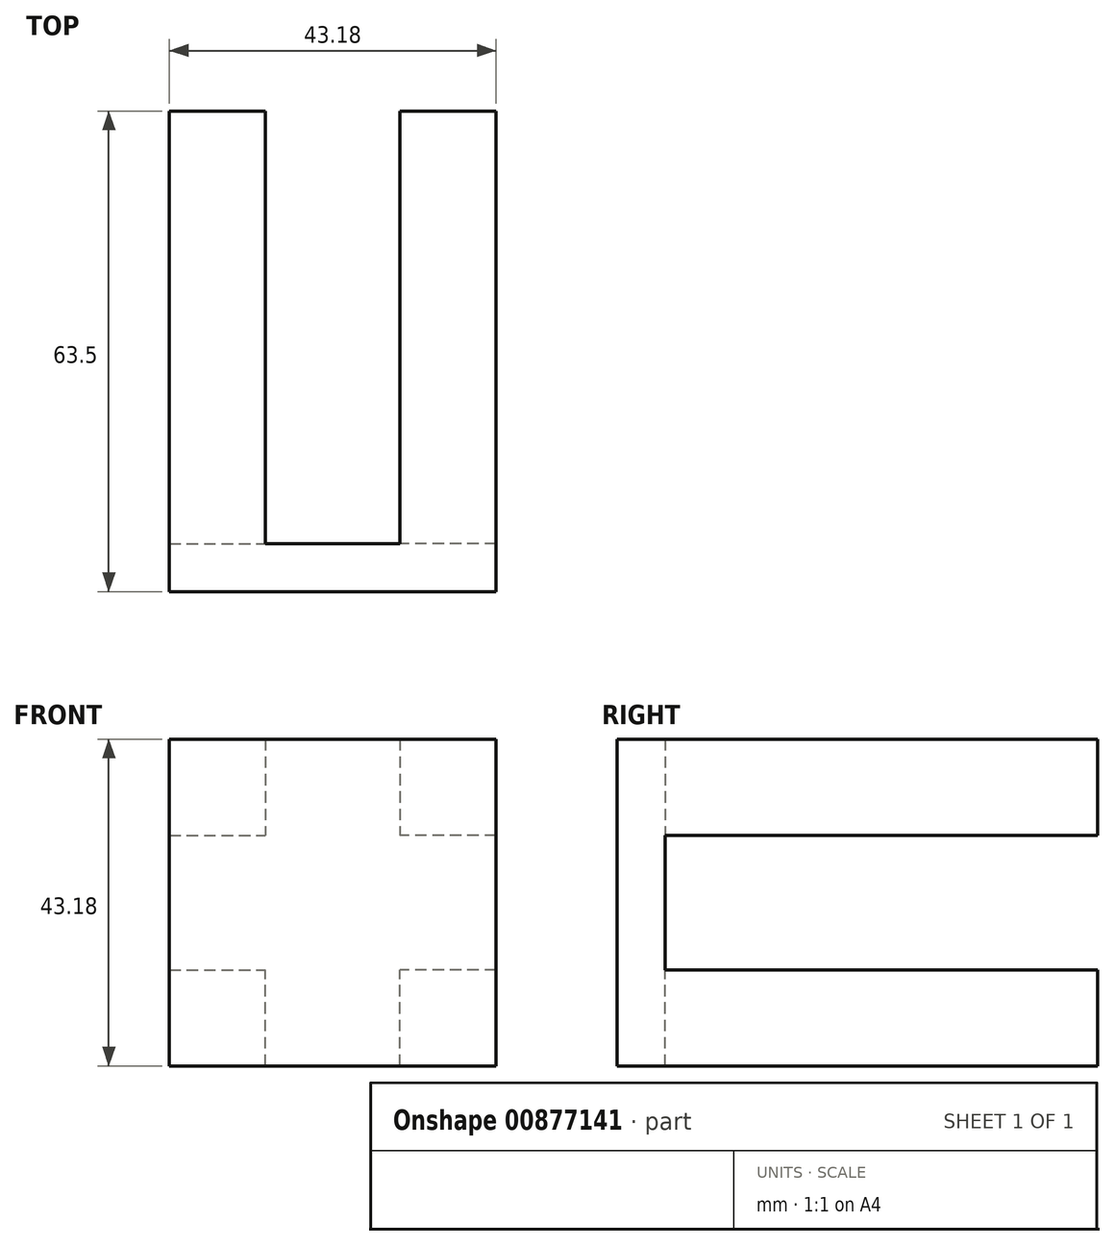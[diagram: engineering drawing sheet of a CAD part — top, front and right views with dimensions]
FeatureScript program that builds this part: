
annotation { "Feature Type Name" : "Feature", "Feature Type Description" : "" }
export const myFeature = defineFeature(function(context is Context, id is Id, definition is map)
    precondition{}
    {
        {
            var Q0;
            Q0=qCreatedBy(makeId("Front.planeOp"),FACE);
            var sketch = newSketch(context, id + "F0", { "sketchPlane" : qUnion([Q0])});
            skLineSegment(sketch, "E0.bottom", {"start": v(-131.6, 23.95) * mm, "end": v(-110, 23.95) * mm});
            skLineSegment(sketch, "E0.top", {"start": v(-131.6, -19.23) * mm, "end": v(-110, -19.23) * mm});
            skLineSegment(sketch, "E0.left", {"start": v(-131.6, 23.95) * mm, "end": v(-131.6, -19.23) * mm});
            skLineSegment(sketch, "E1.bottom", {"start": v(-131.6, 23.95) * mm, "end": v(-118.9, 23.95) * mm});
            skLineSegment(sketch, "E1.top", {"start": v(-131.6, 11.25) * mm, "end": v(-118.9, 11.25) * mm});
            skLineSegment(sketch, "E1.left", {"start": v(-131.6, 23.95) * mm, "end": v(-131.6, 11.25) * mm});
            skLineSegment(sketch, "E1.right", {"start": v(-118.9, 23.95) * mm, "end": v(-118.9, 11.25) * mm});
            skLineSegment(sketch, "E2.bottom", {"start": v(-131.6, -19.23) * mm, "end": v(-118.9, -19.23) * mm});
            skLineSegment(sketch, "E2.top", {"start": v(-131.6, -6.53) * mm, "end": v(-118.9, -6.53) * mm});
            skLineSegment(sketch, "E2.left", {"start": v(-131.6, -19.23) * mm, "end": v(-131.6, -6.53) * mm});
            skLineSegment(sketch, "E2.right", {"start": v(-118.9, -19.23) * mm, "end": v(-118.9, -6.53) * mm});
            skLineSegment(sketch, "E3.MirrorCS", {"start": v(-88.41, 23.95) * mm, "end": v(-88.41, 11.25) * mm});
            skLineSegment(sketch, "E4.MirrorCS", {"start": v(-88.41, -19.23) * mm, "end": v(-88.41, -6.53) * mm});
            skLineSegment(sketch, "E5.MirrorCS", {"start": v(-88.41, -6.53) * mm, "end": v(-101.11, -6.53) * mm});
            skLineSegment(sketch, "E6.MirrorCS", {"start": v(-88.41, -19.23) * mm, "end": v(-101.11, -19.23) * mm});
            skLineSegment(sketch, "E7.MirrorCS", {"start": v(-101.11, -19.23) * mm, "end": v(-101.11, -6.53) * mm});
            skLineSegment(sketch, "E8.MirrorCS", {"start": v(-88.41, 23.95) * mm, "end": v(-88.41, -19.23) * mm});
            skLineSegment(sketch, "E9.MirrorCS", {"start": v(-101.11, 23.95) * mm, "end": v(-101.11, 11.25) * mm});
            skLineSegment(sketch, "E10.MirrorCS", {"start": v(-88.41, -19.23) * mm, "end": v(-110, -19.23) * mm});
            skLineSegment(sketch, "E11.MirrorCS", {"start": v(-88.41, 11.25) * mm, "end": v(-101.11, 11.25) * mm});
            skLineSegment(sketch, "E12.MirrorCS", {"start": v(-88.41, 23.95) * mm, "end": v(-110, 23.95) * mm});
            skLineSegment(sketch, "E13.MirrorCS", {"start": v(-88.41, 23.95) * mm, "end": v(-101.11, 23.95) * mm});
            skSolve(sketch);
        }
        {
            var Q0;
            {var subQ8=sQuery(id+"F0.wireOp",EDGE,"E1.top");Q0=makeQuery(id+"F0.imprint","IMPRINT",FACE,{"disambiguationData":[TD([[makeQuery(id+"F0.imprint","IMPRINT",EDGE,{"derivedFrom":subQ8}),-1.0]])]});}
            extrude(context, id + "F1", {"entities" : qUnion([Q0]), "depth" : 6.35 * mm, "offsetDistance" : 25.4 * mm});
        }
        {
            var Q0;
            Q0=makeQuery(id+"F1.opExtrude","CAP_FACE",FACE,{"disambiguationData":[OSD([sQuery(id+"F0.wireOp",EDGE,"E0.bottom"),sQuery(id+"F0.wireOp",EDGE,"E0.top"),sQuery(id+"F0.wireOp",EDGE,"E0.left"),sQuery(id+"F0.wireOp",EDGE,"E1.top"),sQuery(id+"F0.wireOp",EDGE,"E1.right"),sQuery(id+"F0.wireOp",EDGE,"E2.top"),sQuery(id+"F0.wireOp",EDGE,"E2.right"),sQuery(id+"F0.wireOp",EDGE,"E5.MirrorCS"),sQuery(id+"F0.wireOp",EDGE,"E7.MirrorCS"),sQuery(id+"F0.wireOp",EDGE,"E8.MirrorCS"),sQuery(id+"F0.wireOp",EDGE,"E9.MirrorCS"),sQuery(id+"F0.wireOp",EDGE,"E10.MirrorCS"),sQuery(id+"F0.wireOp",EDGE,"E11.MirrorCS"),sQuery(id+"F0.wireOp",EDGE,"E12.MirrorCS")])],"isStart":false});
            var sketch = newSketch(context, id + "F2", { "sketchPlane" : qUnion([Q0])});
            skLineSegment(sketch, "E14.bottom", {"start": v(-118.9, 11.25) * mm, "end": v(-131.6, 11.25) * mm});
            skLineSegment(sketch, "E14.top", {"start": v(-118.9, 23.95) * mm, "end": v(-131.6, 23.95) * mm});
            skLineSegment(sketch, "E14.left", {"start": v(-118.9, 11.25) * mm, "end": v(-118.9, 23.95) * mm});
            skLineSegment(sketch, "E14.right", {"start": v(-131.6, 11.25) * mm, "end": v(-131.6, 23.95) * mm});
            skLineSegment(sketch, "E15.bottom", {"start": v(-101.11, 23.95) * mm, "end": v(-88.41, 23.95) * mm});
            skLineSegment(sketch, "E15.top", {"start": v(-101.11, 11.25) * mm, "end": v(-88.41, 11.25) * mm});
            skLineSegment(sketch, "E15.left", {"start": v(-101.11, 23.95) * mm, "end": v(-101.11, 11.25) * mm});
            skLineSegment(sketch, "E15.right", {"start": v(-88.41, 23.95) * mm, "end": v(-88.41, 11.25) * mm});
            skLineSegment(sketch, "E16.bottom", {"start": v(-88.41, -19.23) * mm, "end": v(-101.11, -19.23) * mm});
            skLineSegment(sketch, "E16.top", {"start": v(-88.41, -6.53) * mm, "end": v(-101.11, -6.53) * mm});
            skLineSegment(sketch, "E16.left", {"start": v(-88.41, -19.23) * mm, "end": v(-88.41, -6.53) * mm});
            skLineSegment(sketch, "E16.right", {"start": v(-101.11, -19.23) * mm, "end": v(-101.11, -6.53) * mm});
            skLineSegment(sketch, "E17.bottom", {"start": v(-118.9, -19.23) * mm, "end": v(-131.6, -19.23) * mm});
            skLineSegment(sketch, "E17.top", {"start": v(-118.9, -6.53) * mm, "end": v(-131.6, -6.53) * mm});
            skLineSegment(sketch, "E17.left", {"start": v(-118.9, -19.23) * mm, "end": v(-118.9, -6.53) * mm});
            skLineSegment(sketch, "E17.right", {"start": v(-131.6, -19.23) * mm, "end": v(-131.6, -6.53) * mm});
            skSolve(sketch);
        }
        {
            var Q0;
            Q0 = qSketchRegion(id + "F2", true);
            extrude(context, id + "F3", {"entities" : qUnion([Q0]), "operationType" : NewBodyOperationType.ADD, "oppositeDirection" : true, "depth" : 63.5 * mm, "offsetDistance" : 25.4 * mm});
        }
    });
